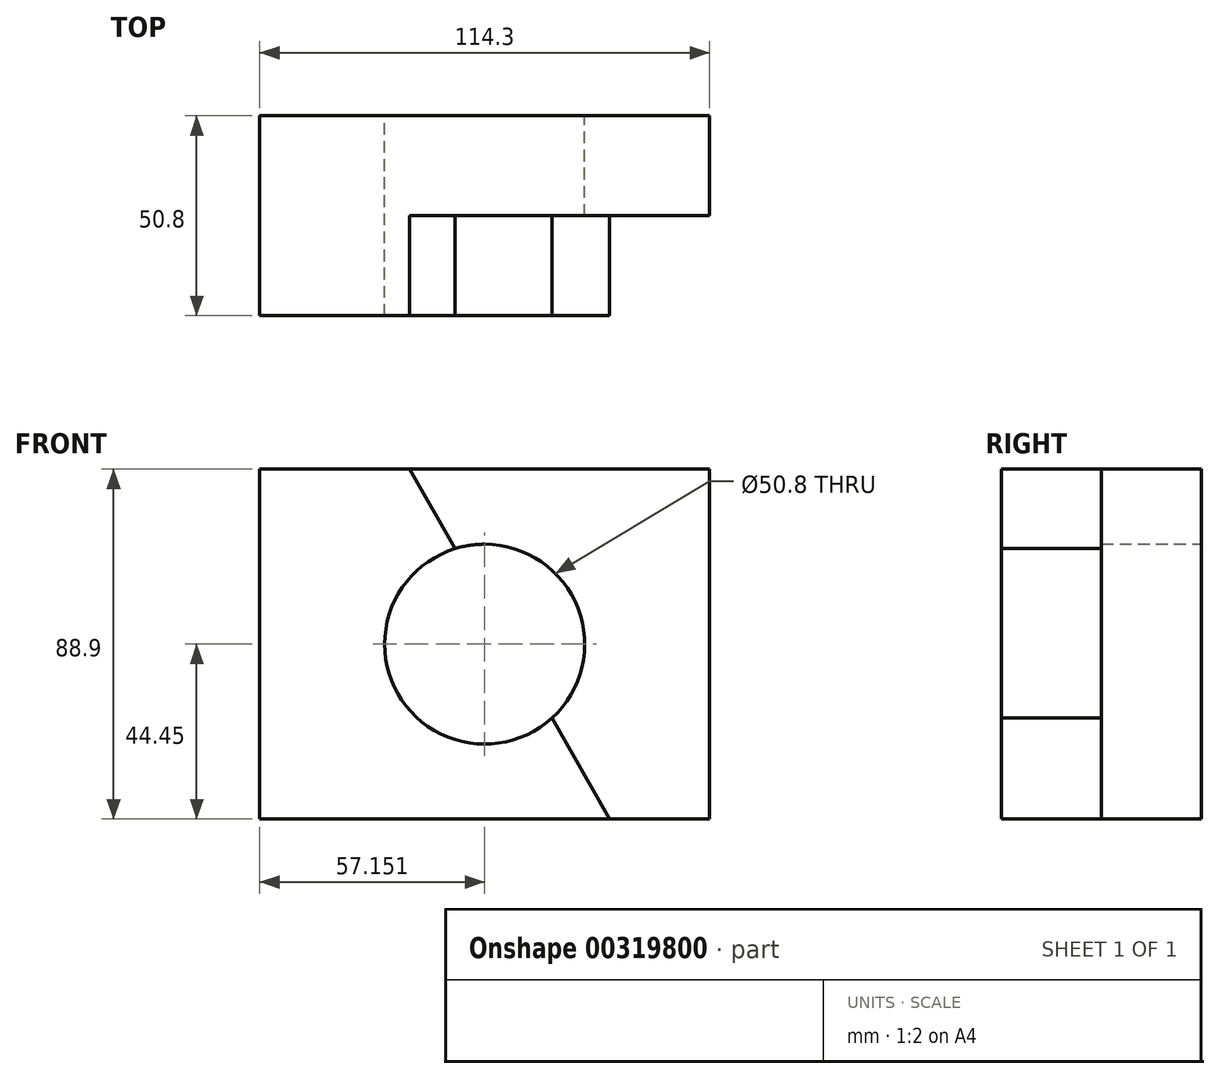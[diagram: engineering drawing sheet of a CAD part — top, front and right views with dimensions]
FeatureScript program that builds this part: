
annotation { "Feature Type Name" : "Feature", "Feature Type Description" : "" }
export const myFeature = defineFeature(function(context is Context, id is Id, definition is map)
    precondition{}
    {
        {
            var Q0;
            Q0=qCreatedBy(makeId("Top.planeOp"),FACE);
            var sketch = newSketch(context, id + "F0", { "sketchPlane" : qUnion([Q0])});
            skLineSegment(sketch, "E0.bottom", {"start": v(-118.8, 29.14) * mm, "end": v(-4.5, 29.14) * mm});
            skLineSegment(sketch, "E0.top", {"start": v(-118.8, 3.74) * mm, "end": v(-4.5, 3.74) * mm});
            skLineSegment(sketch, "E0.left", {"start": v(-118.8, 29.14) * mm, "end": v(-118.8, 3.74) * mm});
            skLineSegment(sketch, "E0.right", {"start": v(-4.5, 29.14) * mm, "end": v(-4.5, 3.74) * mm});
            skSolve(sketch);
        }
        {
            var Q0;
            Q0=makeQuery(id+"F0.imprint","IMPRINT",FACE,{"disambiguationData":[TD([[makeQuery(id+"F0.imprint","IMPRINT",EDGE,{"derivedFrom":sQuery(id+"F0.wireOp",EDGE,"E0.bottom")}),-1.0]])]});
            extrude(context, id + "F1", {"entities" : qUnion([Q0]), "depth" : 88.9 * mm});
        }
        {
            var Q0;
            Q0=makeQuery(id+"F1.opExtrude","SWEPT_FACE",FACE,{"disambiguationData":[OSD([sQuery(id+"F0.wireOp",EDGE,"E0.top")])]});
            var sketch = newSketch(context, id + "F2", { "sketchPlane" : qUnion([Q0])});
            skLineSegment(sketch, "E1", {"start": v(-80.7, 88.9) * mm, "end": v(-118.8, 88.9) * mm});
            skLineSegment(sketch, "E2", {"start": v(-118.8, 88.9) * mm, "end": v(-118.8, 0) * mm});
            skLineSegment(sketch, "E3", {"start": v(-118.8, 0) * mm, "end": v(-29.9, 0) * mm});
            skLineSegment(sketch, "E4", {"start": v(-29.9, 0) * mm, "end": v(-80.7, 88.9) * mm});
            skSolve(sketch);
        }
        {
            var Q0;
            Q0=makeQuery(id+"F2.imprint","IMPRINT",FACE,{"disambiguationData":[TD([[makeQuery(id+"F2.imprint","IMPRINT",EDGE,{"derivedFrom":sQuery(id+"F2.wireOp",EDGE,"E1")}),-1.0]])]});
            extrude(context, id + "F3", {"entities" : qUnion([Q0]), "operationType" : NewBodyOperationType.ADD, "depth" : 25.4 * mm});
        }
        {
            var Q0;
            Q0=makeQuery(id+"F1.opExtrude","SWEPT_FACE",FACE,{"disambiguationData":[OSD([sQuery(id+"F0.wireOp",EDGE,"E0.bottom")])]});
            var sketch = newSketch(context, id + "F4", { "sketchPlane" : qUnion([Q0])});
            skLineSegment(sketch, "E5", {"start": v(4.5, 88.9) * mm, "end": v(118.8, 88.9) * mm});
            skLineSegment(sketch, "E6", {"start": v(118.8, 88.9) * mm, "end": v(118.8, 0) * mm});
            skCircle(sketch, "E7", {"center": v(61.65, 44.45) * mm, "radius": 25.4 * mm});
            skPoint(sketch, "E7.centerSnap0", {"position": v(118.8, 44.45) * mm});
            skPoint(sketch, "E7.centerSnap1", {"position": v(61.65, 88.9) * mm});
            skSolve(sketch);
        }
        {
            var Q0;
            Q0=makeQuery(id+"F4.imprint","IMPRINT",FACE,{"disambiguationData":[TD([[makeQuery(id+"F4.imprint","IMPRINT",EDGE,{"derivedFrom":sQuery(id+"F4.wireOp",EDGE,"E7")}),1.0]])]});
            extrude(context, id + "F5", {"entities" : qUnion([Q0]), "operationType" : NewBodyOperationType.REMOVE, "endBound" : BoundingType.THROUGH_ALL, "oppositeDirection" : true, "depth" : 25.4 * mm});
        }
    });
